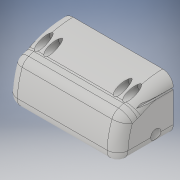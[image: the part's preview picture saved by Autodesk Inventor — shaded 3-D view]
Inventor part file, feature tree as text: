
AUTODESK INVENTOR PART (.ipt)
format: ipt  version: 2017 (Build 210142000, 142)  size: 288,256 bytes
history: native  units: in
note: dims shown in document units (in); Inventor stores cm internally (conversion verified against a paired STEP export)
features: sketch x7, extrude x4, hole x3, fillet x2, plane x1, projected_geometry x1
ambient origin geometry x8: Origin, YZ Plane, XZ Plane, XY Plane, X Axis, Y Axis, Z Axis, Center Point
bodies: Solid1 (feature_tree)
feature tree (18):
  extrude  "Extrusion1"  Depth=1.53in
  fillet  "Fillet5"  Radius=1.6in
  extrude  "Extrusion2"  Depth=1.4in
  fillet  "Fillet6"  Radius=1.1in
  plane  "Work Plane1"
  hole  "Hole1"  [1 undecoded]
  hole  "Hole2"  [1 undecoded]
  hole  "Hole3"  [1 undecoded]
  extrude  "Extrusion3"  Depth=1.6in
  extrude  "Extrusion4"  Depth=0.06in
  sketch  "Sketch1"  dims[d0=3.17in d1=1.53in d2=1.6in d3=0.0in]
  sketch  "Sketch5"  dims[d11=0.3in d12=1.4in d13=1.1in]
  sketch  "Sketch6"  dims[d14=1.25in d15=1.15in]
  sketch  "Sketch7"  dims[d16=0.2in d17=0.3in]
  sketch  "Sketch8"  dims[d18=2.3007in d19=3.7in d20=0.0in]
  sketch  "Sketch9"  dims[d21=0.3in d22=1.6in]
  projected_geometry  "Projected Loop1"
  sketch  "Sketch10"  dims[d23=0.32in d24=0.27in d25=0.18in d26=0.18in d27=0.32in d28=0.27in d29=0.18in d30=0.18in d31=0.2in d32=0.75in d33=0.375in d34=0.25in d35=0.5635in d36=1.0in d37=0.8108in d40=0.3in d41=0.5in d42=0.29in d43=0.75in d44=0.375in d45=0.25in d46=0.5635in d47=0.35in d48=0.8108in d49=0.29in d50=0.75in d51=0.375in d52=0.25in d53=0.5635in d54=0.35in d55=0.8108in d56=0.39in d57=0.39in d58=0.3in d59=0.3in d60=0.2in d61=0.57in d62=0.0in d63=0.3in d64=0.06in d65=0.06in d66=0.3in d67=0.06in d69=0.06in d70=0.57in d71=0.0in]
note: 3 required parameter values undecoded (feature->parameter linkage not recoverable at this tier; creation-order binding heuristic only, values carry confidence <= 0.55)
